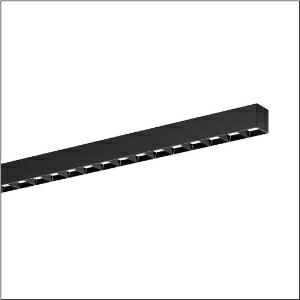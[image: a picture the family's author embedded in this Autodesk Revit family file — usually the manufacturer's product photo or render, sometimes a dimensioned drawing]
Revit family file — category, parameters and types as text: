
# Revit family: silica_r__21_51mx22dc3abb_349a
name_source: partatom
category: Lighting Fixtures
units: mm (PartAtom-declared; Revit-internal decimal feet)

## family parameters
Cut with Voids When Loaded = No
Host = Face
Light Source = No
Part Type = Normal
Room Calculation Point = No
Round Connector Dimension = Use Diameter
Shared = No

## types (1)
- --- (1 x LED, 10800 lm, 69.2 W, 3000K)
    Apparent Load = 69 VA
    CIE Flux Codes = 86 100 100 100 100
    Color Rendering = 80
    Color Temperature = 3000K
    Default Elevation = 1800 mm
    Description = Silica® 21, office luminaire, primary light control with darklight reflector, of PMMA, black, CAT 2 (L<= 3000cd/m²), light emission: direct distribution, primary light characteristic: symmetric, installation type: surface-mounted, LED, rated luminous flux: 10.800lm, luminous efficacy: 156lm/W, light colour: 830, colour temperature: 3000K, with terminal, 3+2-pole, max. 2.5mm², mains connection: 220..240V, AC, 50/60Hz, rated input power: 69.2W, luminaire housing, of aluminium, jet black (RAL 9005), length: 3.004mm, width: 53mm, height: 53mm, protection rating (complete): IP20, insulation class (complete): insulation class I (protective earthing), certification: CE, permissible operating ambient temperature: 0..+35°C, standard: EN 50419, packaging unit: 1 piece
    Height = 0 mm  [stored 0 ft]
    Lamp = 1 x LED
    Lamp Light Flux = 10800 lm
    Lamp Power = 69.2 W
    Lamp count = 1
    Length = 3004 mm
    Luminous efficacy = 156 lm/W
    Manufacturer = Siteco
    ModVariant = No
    Model = 51MX22DC3ABB
    Mounting Place = Ceiling
    Mounting Type = Recessed
    Number of Poles = 1
    OnlyDefault = Yes
    Power Factor = 1
    Product Name = Silica® 21
    Product group = office luminaire | ceiling recessed
    ProductGroupID = 401
    Protection Class = Protection class I
    Protection Degree = IP 20
    RLX_Detail_Level = 1
    RLX_Emergency_Light_Flux = 0 lm
    RLX_Emergency_Type = 0
    RLX_Emergency_Type_DB = No
    RlxData = <blob elided: 63457 chars, md5=befc27b1>
    Socket = socket
    Standby Power = 0 W
    System Light Flux = 10800 lm
    System Power = 69 W
    Type Comments = factory setting: luminous flux: 100 % | dim-lin: 254 | 392 mA
    Type Image = l_1297756.jpg
    URL = http://relux.com
    VarID = @adj_056039
    Voltage = 0 V
    Weight = 0.00 kg
    Width = 53 mm

note: [stored X ft] marks values corroborated as IEEE doubles in the binary element streams (Revit-internal decimal feet)

## geometry (parser evidence)
native form markers: Blend x4, Sweep x10
no freeform markers — native parametric forms only
